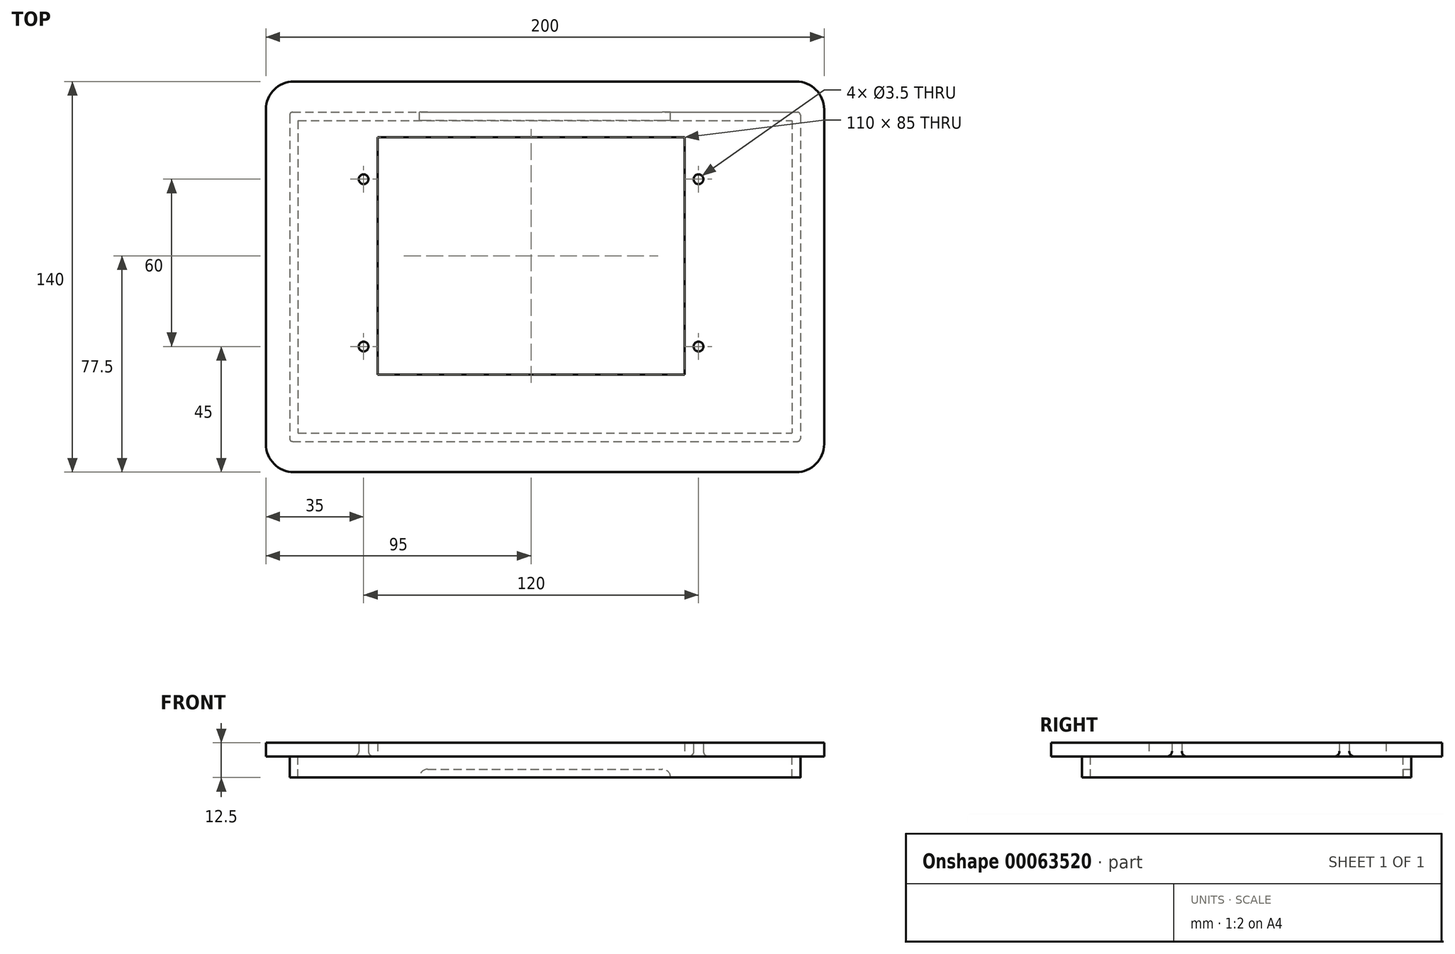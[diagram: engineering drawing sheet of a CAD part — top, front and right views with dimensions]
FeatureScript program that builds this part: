
annotation { "Feature Type Name" : "Feature", "Feature Type Description" : "" }
export const myFeature = defineFeature(function(context is Context, id is Id, definition is map)
    precondition{}
    {
        {
            var Q0;
            Q0=qCreatedBy(makeId("Top.planeOp"),FACE);
            var sketch = newSketch(context, id + "F0", { "sketchPlane" : qUnion([Q0])});
            skLineSegment(sketch, "E0.rect.bottom", {"start": v(-100, 70) * mm, "end": v(100, 70) * mm});
            skLineSegment(sketch, "E0.rect.top", {"start": v(-100, -70) * mm, "end": v(100, -70) * mm});
            skLineSegment(sketch, "E0.rect.left", {"start": v(-100, 70) * mm, "end": v(-100, -70) * mm});
            skLineSegment(sketch, "E0.rect.right", {"start": v(100, 70) * mm, "end": v(100, -70) * mm});
            skPoint(sketch, "E0.rect.middle", {"position": v(0, 0) * mm});
            skLineSegment(sketch, "E1.rect.bottom", {"start": v(-91.5, 59) * mm, "end": v(91.5, 59) * mm});
            skLineSegment(sketch, "E1.rect.top", {"start": v(-91.5, -59) * mm, "end": v(91.5, -59) * mm});
            skLineSegment(sketch, "E1.rect.left", {"start": v(-91.5, 59) * mm, "end": v(-91.5, -59) * mm});
            skLineSegment(sketch, "E1.rect.right", {"start": v(91.5, 59) * mm, "end": v(91.5, -59) * mm});
            skLineSegment(sketch, "E2.rect.bottom", {"start": v(-88.5, 56) * mm, "end": v(88.5, 56) * mm});
            skLineSegment(sketch, "E2.rect.top", {"start": v(-88.5, -56) * mm, "end": v(88.5, -56) * mm});
            skLineSegment(sketch, "E2.rect.left", {"start": v(-88.5, 56) * mm, "end": v(-88.5, -56) * mm});
            skLineSegment(sketch, "E2.rect.right", {"start": v(88.5, 56) * mm, "end": v(88.5, -56) * mm});
            skLineSegment(sketch, "E3.bottom", {"start": v(-60, -35) * mm, "end": v(50, -35) * mm});
            skLineSegment(sketch, "E3.top", {"start": v(-60, 50) * mm, "end": v(50, 50) * mm});
            skLineSegment(sketch, "E3.left", {"start": v(-60, -35) * mm, "end": v(-60, 50) * mm});
            skLineSegment(sketch, "E3.right", {"start": v(50, -35) * mm, "end": v(50, 50) * mm});
            skLineSegment(sketch, "E4", {"start": v(-105.24, 0) * mm, "end": v(108.88, 0) * mm, "construction": true});
            skPoint(sketch, "E4.startSnap0", {"position": v(-100, 0) * mm});
            skPoint(sketch, "E4.endSnap0", {"position": v(100, 0) * mm});
            skLineSegment(sketch, "E5", {"start": v(0, 70) * mm, "end": v(0, -70) * mm, "construction": true});
            skCircle(sketch, "E6", {"center": v(-65, 35) * mm, "radius": 1.75 * mm});
            skCircle(sketch, "E7", {"center": v(55, 35) * mm, "radius": 1.75 * mm});
            skCircle(sketch, "E8", {"center": v(55, -25) * mm, "radius": 1.75 * mm});
            skCircle(sketch, "E9", {"center": v(-65, -25) * mm, "radius": 1.75 * mm});
            skSolve(sketch);
        }
        {
            var Q0;
            Q0=makeQuery(id+"F0.imprint","IMPRINT",FACE,{"disambiguationData":[TD([[makeQuery(id+"F0.imprint","IMPRINT",EDGE,{"derivedFrom":sQuery(id+"F0.wireOp",EDGE,"E0.rect.bottom")}),-1.0]])]});
            var Q1;
            Q1=makeQuery(id+"F0.imprint","IMPRINT",FACE,{"disambiguationData":[TD([[makeQuery(id+"F0.imprint","IMPRINT",EDGE,{"derivedFrom":sQuery(id+"F0.wireOp",EDGE,"E2.rect.bottom")}),-1.0]])]});
            var Q2;
            Q2=makeQuery(id+"F0.imprint","IMPRINT",FACE,{"disambiguationData":[TD([[makeQuery(id+"F0.imprint","IMPRINT",EDGE,{"derivedFrom":sQuery(id+"F0.wireOp",EDGE,"E1.rect.bottom")}),-1.0]])]});
            extrude(context, id + "F1", {"entities" : qUnion([Q0, Q1, Q2]), "depth" : 5 * mm});
        }
        {
            var Q0;
            Q0=makeQuery(id+"F0.imprint","IMPRINT",FACE,{"disambiguationData":[TD([[makeQuery(id+"F0.imprint","IMPRINT",EDGE,{"derivedFrom":sQuery(id+"F0.wireOp",EDGE,"E1.rect.bottom")}),-1.0]])]});
            extrude(context, id + "F2", {"entities" : qUnion([Q0]), "operationType" : NewBodyOperationType.ADD, "oppositeDirection" : true, "depth" : 7.5 * mm});
        }
        {
            var Q0;
            Q0=makeQuery(id+"F1.opExtrude","SWEPT_EDGE",EDGE,{"disambiguationData":[OSD([sQuery(id+"F0.wireOp",EDGE,"E0.rect.bottom"),sQuery(id+"F0.wireOp",EDGE,"E0.rect.left")])]});
            var Q1;
            Q1=makeQuery(id+"F1.opExtrude","SWEPT_EDGE",EDGE,{"disambiguationData":[OSD([sQuery(id+"F0.wireOp",EDGE,"E0.rect.top"),sQuery(id+"F0.wireOp",EDGE,"E0.rect.left")])]});
            var Q2;
            Q2=makeQuery(id+"F1.opExtrude","SWEPT_EDGE",EDGE,{"disambiguationData":[OSD([sQuery(id+"F0.wireOp",EDGE,"E0.rect.top"),sQuery(id+"F0.wireOp",EDGE,"E0.rect.right")])]});
            var Q3;
            Q3=makeQuery(id+"F1.opExtrude","SWEPT_EDGE",EDGE,{"disambiguationData":[OSD([sQuery(id+"F0.wireOp",EDGE,"E0.rect.bottom"),sQuery(id+"F0.wireOp",EDGE,"E0.rect.right")])]});
            fillet(context, id + "F3", {"entities" : qUnion([Q0, Q1, Q2, Q3]), "radius" : 10 * mm, "tangentPropagation" : true, "allowEdgeOverflow" : false});
        }
        {
            var Q0;
            Q0=makeQuery(id+"F2.opExtrude","SWEPT_EDGE",EDGE,{"disambiguationData":[OSD([sQuery(id+"F0.wireOp",EDGE,"E1.rect.top"),sQuery(id+"F0.wireOp",EDGE,"E1.rect.left")])]});
            var Q1;
            Q1=makeQuery(id+"F2.opExtrude","SWEPT_EDGE",EDGE,{"disambiguationData":[OSD([sQuery(id+"F0.wireOp",EDGE,"E1.rect.top"),sQuery(id+"F0.wireOp",EDGE,"E1.rect.right")])]});
            var Q2;
            Q2=makeQuery(id+"F2.opExtrude","SWEPT_EDGE",EDGE,{"disambiguationData":[OSD([sQuery(id+"F0.wireOp",EDGE,"E1.rect.bottom"),sQuery(id+"F0.wireOp",EDGE,"E1.rect.left")])]});
            var Q3;
            Q3=makeQuery(id+"F2.opExtrude","SWEPT_EDGE",EDGE,{"disambiguationData":[OSD([sQuery(id+"F0.wireOp",EDGE,"E1.rect.bottom"),sQuery(id+"F0.wireOp",EDGE,"E1.rect.right")])]});
            fillet(context, id + "F4", {"entities" : qUnion([Q0, Q1, Q2, Q3]), "radius" : 1 * mm, "tangentPropagation" : true, "allowEdgeOverflow" : false});
        }
        {
            var Q0;
            Q0=makeQuery(id+"F1.opExtrude","CAP_EDGE",EDGE,{"disambiguationData":[OSD([sQuery(id+"F0.wireOp",EDGE,"E9")])],"isStart":true});
            var Q1;
            Q1=makeQuery(id+"F1.opExtrude","CAP_EDGE",EDGE,{"disambiguationData":[OSD([sQuery(id+"F0.wireOp",EDGE,"E8")])],"isStart":true});
            var Q2;
            Q2=makeQuery(id+"F1.opExtrude","CAP_EDGE",EDGE,{"disambiguationData":[OSD([sQuery(id+"F0.wireOp",EDGE,"E6")])],"isStart":true});
            var Q3;
            Q3=makeQuery(id+"F1.opExtrude","CAP_EDGE",EDGE,{"disambiguationData":[OSD([sQuery(id+"F0.wireOp",EDGE,"E7")])],"isStart":true});
            fillet(context, id + "F5", {"entities" : qUnion([Q0, Q1, Q2, Q3]), "radius" : 2 * mm, "tangentPropagation" : true, "allowEdgeOverflow" : false});
        }
        {
            var Q0;
            Q0=makeQuery(id+"F2.opExtrude","SWEPT_FACE",FACE,{"disambiguationData":[OSD([sQuery(id+"F0.wireOp",EDGE,"E1.rect.bottom")])]});
            var sketch = newSketch(context, id + "F6", { "sketchPlane" : qUnion([Q0])});
            skLineSegment(sketch, "E10", {"start": v(0, 0) * mm, "end": v(0, -17.87) * mm, "construction": true});
            skPoint(sketch, "E10.endSnap0", {"position": v(0, -7.5) * mm});
            skLineSegment(sketch, "E11.bottom", {"start": v(0, -7.5) * mm, "end": v(45, -7.5) * mm});
            skLineSegment(sketch, "E11.top", {"start": v(0, -4.5) * mm, "end": v(45, -4.5) * mm});
            skLineSegment(sketch, "E11.left", {"start": v(0, -7.5) * mm, "end": v(0, -4.5) * mm});
            skLineSegment(sketch, "E11.right", {"start": v(45, -7.5) * mm, "end": v(45, -4.5) * mm});
            skLineSegment(sketch, "E12.bottom", {"start": v(0, -7.5) * mm, "end": v(-45, -7.5) * mm});
            skLineSegment(sketch, "E12.top", {"start": v(0, -4.5) * mm, "end": v(-45, -4.5) * mm});
            skLineSegment(sketch, "E12.right", {"start": v(-45, -7.5) * mm, "end": v(-45, -4.5) * mm});
            skSolve(sketch);
        }
        {
            var Q0;
            Q0=makeQuery(id+"F6.imprint","IMPRINT",FACE,{"disambiguationData":[TD([[makeQuery(id+"F6.imprint","IMPRINT",EDGE,{"derivedFrom":sQuery(id+"F6.wireOp",EDGE,"E12.bottom")}),-1.0]])]});
            var Q1;
            Q1=makeQuery(id+"F6.imprint","IMPRINT",FACE,{"disambiguationData":[TD([[makeQuery(id+"F6.imprint","IMPRINT",EDGE,{"derivedFrom":sQuery(id+"F6.wireOp",EDGE,"E11.bottom")}),-1.0]])]});
            extrude(context, id + "F7", {"entities" : qUnion([Q0, Q1]), "operationType" : NewBodyOperationType.REMOVE, "oppositeDirection" : true, "depth" : 25 * mm});
        }
        {
            var Q0;
            Q0=makeQuery(id+"F7.boolean.opBoolean","COPY",EDGE,{"derivedFrom":makeQuery(id+"F7.opExtrude","SWEPT_EDGE",EDGE,{"disambiguationData":[OSD([sQuery(id+"F6.wireOp",EDGE,"E11.top"),sQuery(id+"F6.wireOp",EDGE,"E11.right")])]})});
            var Q1;
            Q1=makeQuery(id+"F7.boolean.opBoolean","COPY",EDGE,{"derivedFrom":makeQuery(id+"F7.opExtrude","SWEPT_EDGE",EDGE,{"disambiguationData":[OSD([sQuery(id+"F6.wireOp",EDGE,"E12.top"),sQuery(id+"F6.wireOp",EDGE,"E12.right")])]})});
            fillet(context, id + "F8", {"entities" : qUnion([Q0, Q1]), "radius" : 3 * mm, "tangentPropagation" : true, "allowEdgeOverflow" : false});
        }
    });
